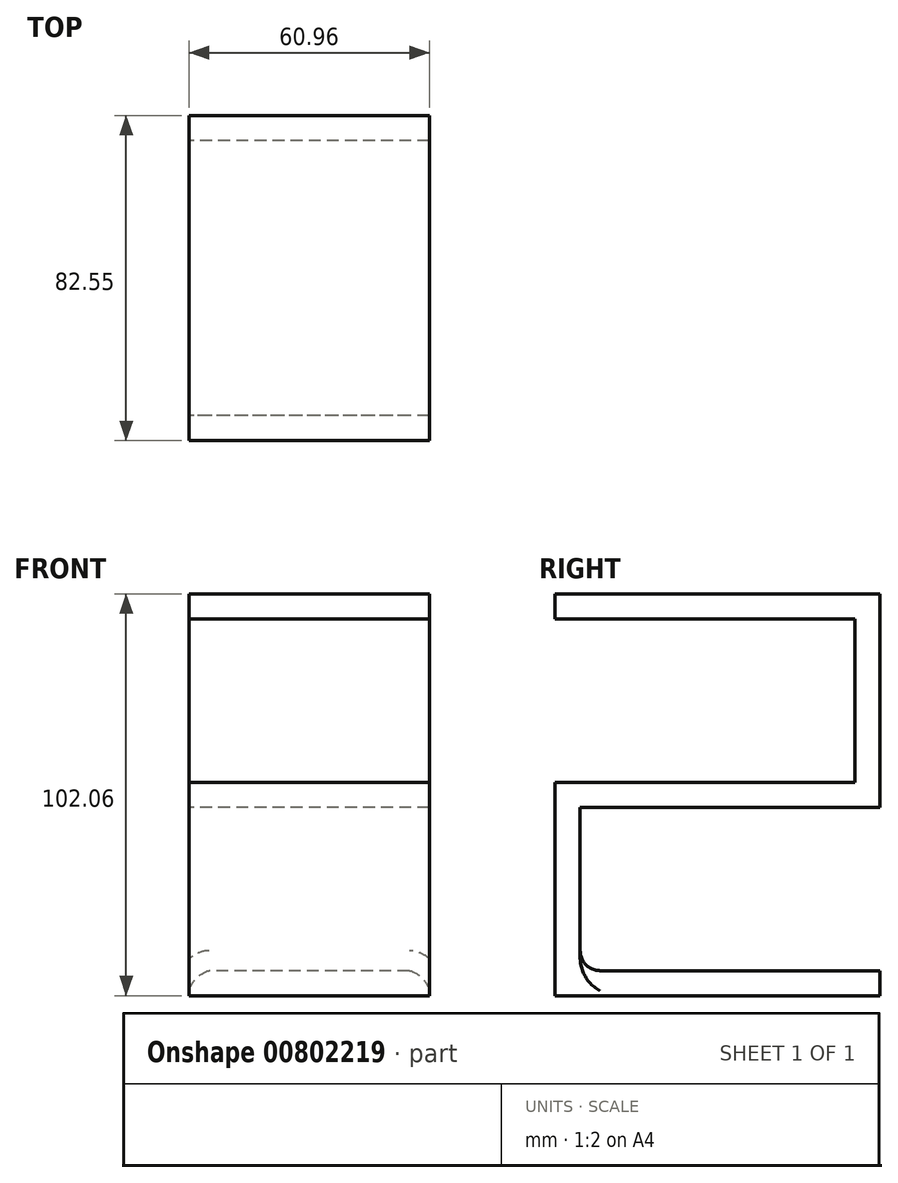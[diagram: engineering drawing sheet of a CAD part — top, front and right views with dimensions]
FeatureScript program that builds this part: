
annotation { "Feature Type Name" : "Feature", "Feature Type Description" : "" }
export const myFeature = defineFeature(function(context is Context, id is Id, definition is map)
    precondition{}
    {
        {
            var Q0;
            Q0=qCreatedBy(makeId("Right.planeOp"),FACE);
            var sketch = newSketch(context, id + "F0", { "sketchPlane" : qUnion([Q0])});
            skLineSegment(sketch, "E0", {"start": v(-38.1, 44.68) * mm, "end": v(38.1, 44.68) * mm});
            skLineSegment(sketch, "E1", {"start": v(38.1, 44.68) * mm, "end": v(38.1, 3.18) * mm});
            skLineSegment(sketch, "E2", {"start": v(38.1, 3.18) * mm, "end": v(-38.1, 3.18) * mm});
            skLineSegment(sketch, "E3", {"start": v(-38.1, 3.18) * mm, "end": v(-38.1, -51.03) * mm});
            skLineSegment(sketch, "E4", {"start": v(-38.1, -51.03) * mm, "end": v(44.45, -51.03) * mm});
            skLineSegment(sketch, "E5", {"start": v(44.45, -51.03) * mm, "end": v(44.45, -44.68) * mm});
            skLineSegment(sketch, "E6", {"start": v(44.45, -44.67) * mm, "end": v(-31.75, -44.68) * mm});
            skLineSegment(sketch, "E7", {"start": v(-31.75, -44.68) * mm, "end": v(-31.75, -3.18) * mm});
            skLineSegment(sketch, "E8", {"start": v(-31.75, -3.18) * mm, "end": v(44.45, -3.18) * mm});
            skLineSegment(sketch, "E9", {"start": v(44.45, -3.17) * mm, "end": v(44.45, 51.03) * mm});
            skLineSegment(sketch, "E10", {"start": v(44.45, 51.03) * mm, "end": v(-38.1, 51.03) * mm});
            skLineSegment(sketch, "E11", {"start": v(-38.1, 51.03) * mm, "end": v(-38.1, 44.67) * mm});
            skLineSegment(sketch, "E12", {"start": v(0, 44.68) * mm, "end": v(0, 3.17) * mm, "construction": true});
            skLineSegment(sketch, "E13", {"start": v(0, -3.17) * mm, "end": v(0, -44.68) * mm, "construction": true});
            skLineSegment(sketch, "E14", {"start": v(0, 44.68) * mm, "end": v(0, 51.03) * mm, "construction": true});
            skLineSegment(sketch, "E15", {"start": v(38.1, 23.93) * mm, "end": v(44.45, 23.93) * mm, "construction": true});
            skLineSegment(sketch, "E16", {"start": v(0, 3.17) * mm, "end": v(0, -3.17) * mm, "construction": true});
            skLineSegment(sketch, "E17", {"start": v(-38.1, -23.93) * mm, "end": v(-31.75, -23.93) * mm, "construction": true});
            skPoint(sketch, "E17.startSnap0", {"position": v(-38.1, -23.93) * mm});
            skPoint(sketch, "E17.startSnap1", {"position": v(-31.75, -23.93) * mm});
            skPoint(sketch, "E17.endSnap0", {"position": v(-38.1, -23.93) * mm});
            skPoint(sketch, "E17.endSnap1", {"position": v(-31.75, -23.93) * mm});
            skLineSegment(sketch, "E18", {"start": v(0, -44.68) * mm, "end": v(0, -51.03) * mm, "construction": true});
            skPoint(sketch, "E19", {"position": v(0, 0) * mm});
            skSolve(sketch);
        }
        {
            var Q0;
            Q0=makeQuery(id+"F0.imprint","IMPRINT",FACE,{"disambiguationData":[TD([[makeQuery(id+"F0.imprint","IMPRINT",EDGE,{"derivedFrom":sQuery(id+"F0.wireOp",EDGE,"E0")}),1.0]])]});
            extrude(context, id + "F1", {"entities" : qUnion([Q0]), "endBound" : BoundingType.SYMMETRIC, "depth" : 60.96 * mm, "offsetDistance" : 25.4 * mm});
        }
        {
            var Q0;
            Q0=makeQuery(id+"F1.opExtrude","CAP_EDGE",EDGE,{"disambiguationData":[OSD([sQuery(id+"F0.wireOp",EDGE,"E6")])],"isStart":false});
            var Q1;
            Q1=makeQuery(id+"F1.opExtrude","CAP_EDGE",EDGE,{"disambiguationData":[OSD([sQuery(id+"F0.wireOp",EDGE,"E6")])],"isStart":true});
            fillet(context, id + "F2", {"entities" : qUnion([Q0, Q1]), "radius" : 5.08 * mm, "tangentPropagation" : true, "rho" : 0.25, "crossSection" : FilletCrossSection.CONIC, "allowEdgeOverflow" : false});
        }
        {
            var Q0;
            Q0=makeQuery(id+"F2.opFillet","BLEND_EDGE",EDGE,{"blendedFrom":[makeQuery(id+"F1.opExtrude","CAP_EDGE",EDGE,{"disambiguationData":[OSD([sQuery(id+"F0.wireOp",EDGE,"E6")])],"isStart":false}),makeQuery(id+"F1.opExtrude","SWEPT_FACE",FACE,{"disambiguationData":[OSD([sQuery(id+"F0.wireOp",EDGE,"E7")])]})],"blendedInto":[makeQuery(id+"F1.opExtrude","SWEPT_FACE",FACE,{"disambiguationData":[OSD([sQuery(id+"F0.wireOp",EDGE,"E7")])]})]});
            var Q1;
            Q1=makeQuery(id+"F1.opExtrude","SWEPT_EDGE",EDGE,{"disambiguationData":[OSD([sQuery(id+"F0.wireOp",EDGE,"E6"),sQuery(id+"F0.wireOp",EDGE,"E7")])]});
            var Q2;
            Q2=makeQuery(id+"F2.opFillet","BLEND_EDGE",EDGE,{"blendedFrom":[makeQuery(id+"F1.opExtrude","CAP_EDGE",EDGE,{"disambiguationData":[OSD([sQuery(id+"F0.wireOp",EDGE,"E6")])],"isStart":true}),makeQuery(id+"F1.opExtrude","SWEPT_FACE",FACE,{"disambiguationData":[OSD([sQuery(id+"F0.wireOp",EDGE,"E7")])]})],"blendedInto":[makeQuery(id+"F1.opExtrude","SWEPT_FACE",FACE,{"disambiguationData":[OSD([sQuery(id+"F0.wireOp",EDGE,"E7")])]})]});
            fillet(context, id + "F3", {"entities" : qUnion([Q0, Q1, Q2]), "radius" : 5.08 * mm, "tangentPropagation" : true, "allowEdgeOverflow" : false});
        }
    });
